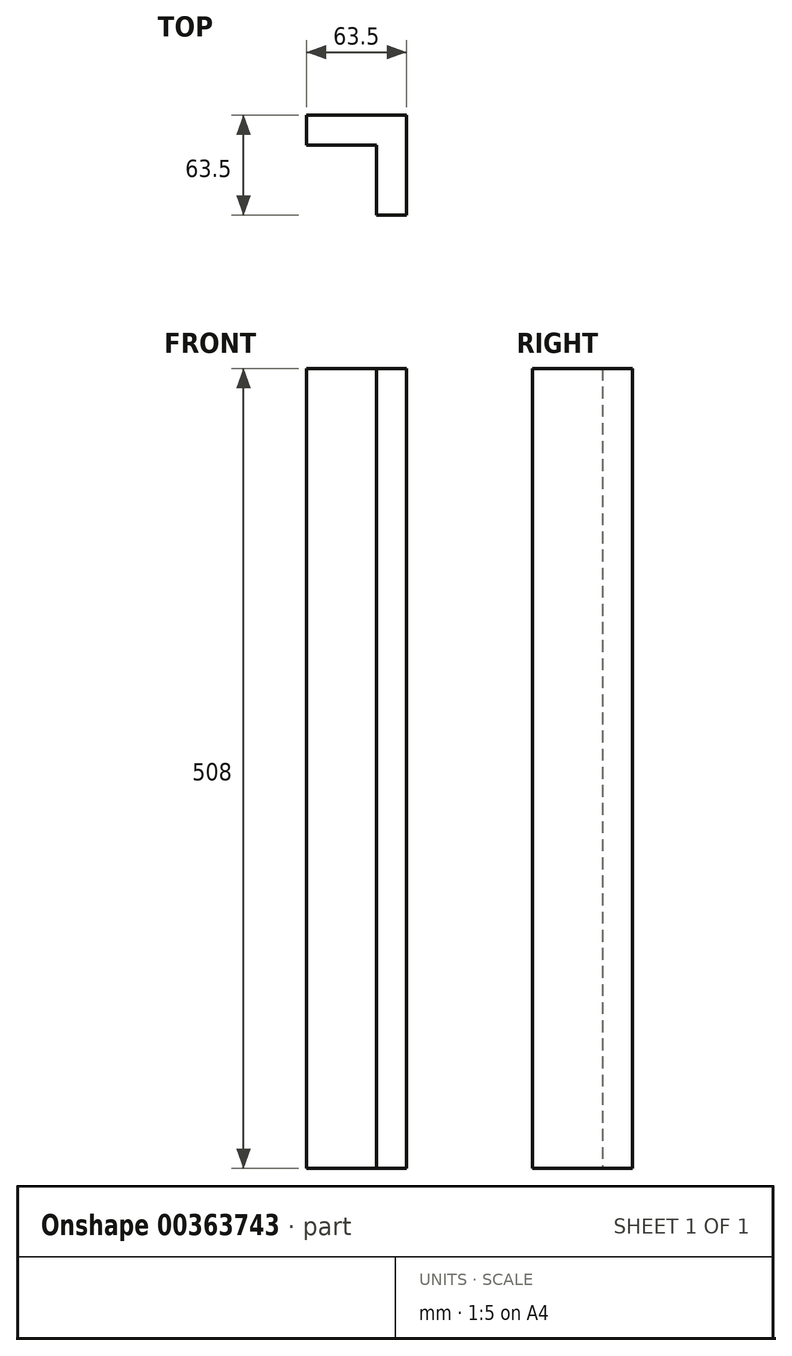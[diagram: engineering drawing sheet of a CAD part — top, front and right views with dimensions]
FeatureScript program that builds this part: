
annotation { "Feature Type Name" : "Feature", "Feature Type Description" : "" }
export const myFeature = defineFeature(function(context is Context, id is Id, definition is map)
    precondition{}
    {
        {
            var Q0;
            Q0=qCreatedBy(makeId("Front.planeOp"),FACE);
            var sketch = newSketch(context, id + "F0", { "sketchPlane" : qUnion([Q0])});
            skLineSegment(sketch, "E0.bottom", {"start": v(31.75, 254) * mm, "end": v(-31.75, 254) * mm});
            skLineSegment(sketch, "E0.top", {"start": v(31.75, -254) * mm, "end": v(-31.75, -254) * mm});
            skLineSegment(sketch, "E0.left", {"start": v(31.75, 254) * mm, "end": v(31.75, -254) * mm});
            skLineSegment(sketch, "E0.right", {"start": v(-31.75, 254) * mm, "end": v(-31.75, -254) * mm});
            skPoint(sketch, "E0.middle", {"position": v(0, 0) * mm});
            skSolve(sketch);
        }
        {
            var Q0;
            Q0 = qSketchRegion(id + "F0", true);
            extrude(context, id + "F1", {"entities" : qUnion([Q0]), "depth" : 19.05 * mm});
        }
        {
            var Q0;
            Q0=makeQuery(id+"F1.opExtrude","SWEPT_FACE",FACE,{"disambiguationData":[OSD([sQuery(id+"F0.wireOp",EDGE,"E0.left")])]});
            var sketch = newSketch(context, id + "F2", { "sketchPlane" : qUnion([Q0])});
            skLineSegment(sketch, "E1.bottom", {"start": v(-19.05, 254) * mm, "end": v(-63.5, 254) * mm});
            skLineSegment(sketch, "E1.top", {"start": v(-19.05, -254) * mm, "end": v(-63.5, -254) * mm});
            skLineSegment(sketch, "E1.left", {"start": v(-19.05, 254) * mm, "end": v(-19.05, -254) * mm});
            skLineSegment(sketch, "E1.right", {"start": v(-63.5, 254) * mm, "end": v(-63.5, -254) * mm});
            skSolve(sketch);
        }
        {
            var Q0;
            Q0=makeQuery(id+"F2.imprint","IMPRINT",FACE,{"disambiguationData":[TD([[makeQuery(id+"F2.imprint","IMPRINT",EDGE,{"derivedFrom":sQuery(id+"F2.wireOp",EDGE,"E1.bottom")}),1.0]])]});
            extrude(context, id + "F3", {"entities" : qUnion([Q0]), "operationType" : NewBodyOperationType.ADD, "oppositeDirection" : true, "depth" : 19.05 * mm});
        }
    });
